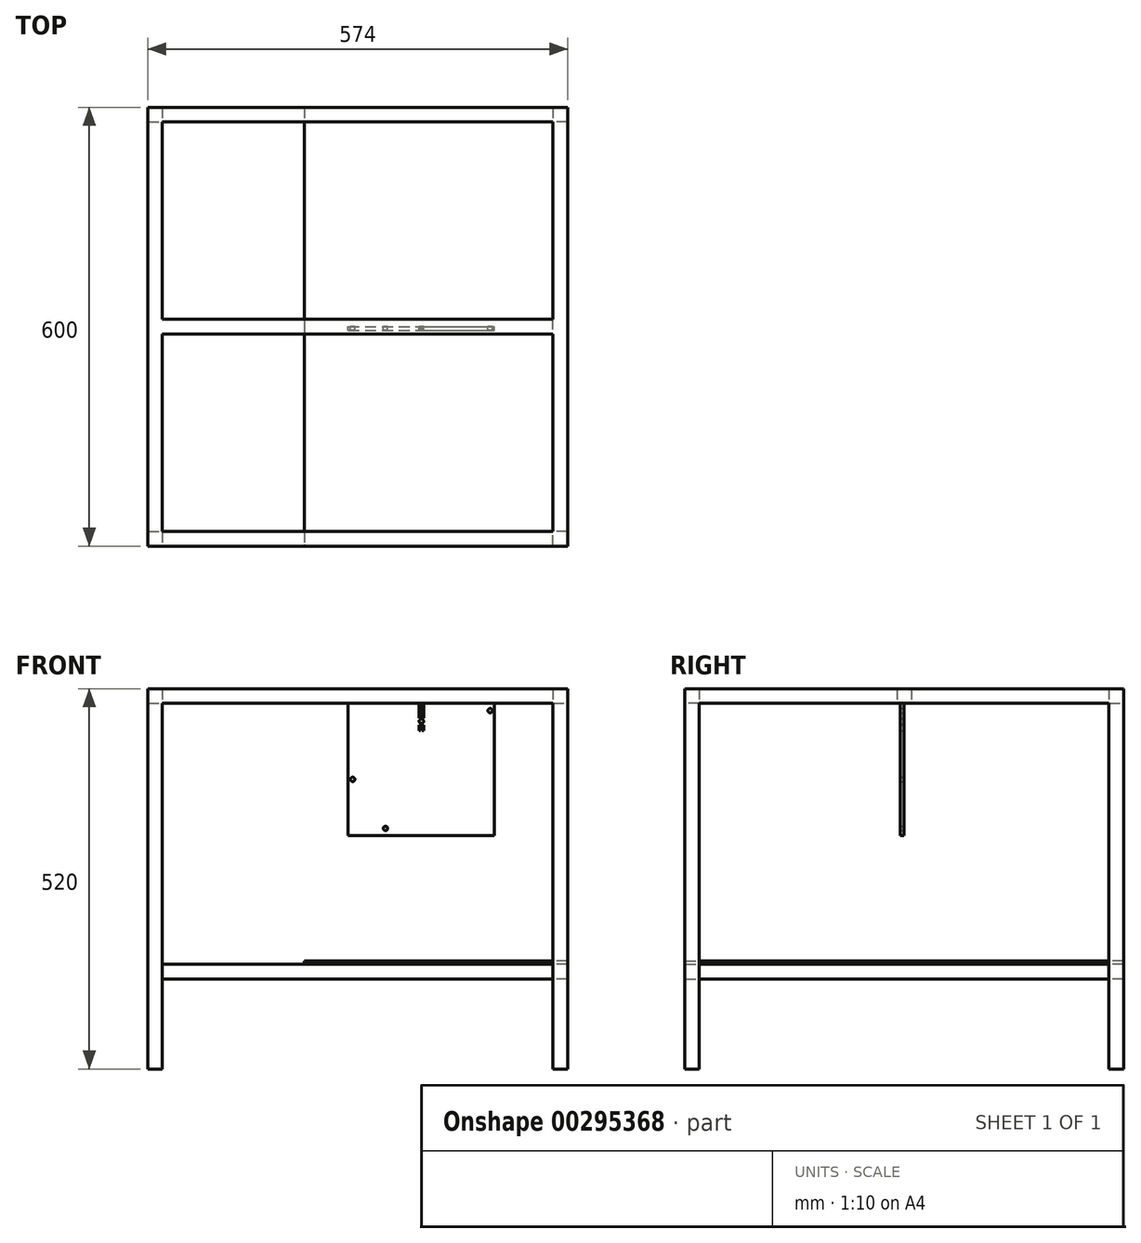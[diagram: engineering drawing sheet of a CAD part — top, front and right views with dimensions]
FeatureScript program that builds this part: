
annotation { "Feature Type Name" : "Feature", "Feature Type Description" : "" }
export const myFeature = defineFeature(function(context is Context, id is Id, definition is map)
    precondition{}
    {
        {
            var Q0;
            Q0=qCreatedBy(makeId("Front.planeOp"),FACE);
            var sketch = newSketch(context, id + "F0", { "sketchPlane" : qUnion([Q0])});
            skCircle(sketch, "E0", {"center": v(0, 0) * mm, "radius": 3 * mm});
            skCircle(sketch, "E1", {"center": v(-45, 67) * mm, "radius": 3 * mm});
            skCircle(sketch, "E2", {"center": v(143, 161) * mm, "radius": 3 * mm});
            skLineSegment(sketch, "E3.bottom", {"start": v(-51, -10) * mm, "end": v(149, -10) * mm});
            skLineSegment(sketch, "E3.top", {"start": v(-51, 171) * mm, "end": v(45.95, 171) * mm});
            skLineSegment(sketch, "E3.left", {"start": v(-51, -10) * mm, "end": v(-51, 171) * mm});
            skLineSegment(sketch, "E3.right", {"start": v(149, -10) * mm, "end": v(149, 171) * mm});
            skCircle(sketch, "E4", {"center": v(49, 146.5) * mm, "radius": 3 * mm});
            skPoint(sketch, "E4.centerSnap0", {"position": v(49, 171) * mm});
            skLineSegment(sketch, "E5.top", {"start": v(45.95, 151) * mm, "end": v(48.05, 151) * mm});
            skLineSegment(sketch, "E5.left", {"start": v(45.95, 171) * mm, "end": v(45.95, 151) * mm});
            skLineSegment(sketch, "E5.right", {"start": v(48.05, 171) * mm, "end": v(48.05, 151) * mm});
            skLineSegment(sketch, "E6.bottom", {"start": v(45.95, 141.5) * mm, "end": v(48.05, 141.5) * mm});
            skLineSegment(sketch, "E6.top", {"start": v(45.95, 133.5) * mm, "end": v(48.05, 133.5) * mm});
            skLineSegment(sketch, "E6.left", {"start": v(45.95, 141.5) * mm, "end": v(45.95, 133.5) * mm});
            skLineSegment(sketch, "E6.right", {"start": v(48.05, 141.5) * mm, "end": v(48.05, 133.5) * mm});
            skLineSegment(sketch, "E7.trimOffspring", {"start": v(48.05, 171) * mm, "end": v(149, 171) * mm});
            skLineSegment(sketch, "E8.MirrorCS", {"start": v(52.05, 133.5) * mm, "end": v(49.95, 133.5) * mm});
            skLineSegment(sketch, "E9.MirrorCS", {"start": v(52.05, 141.5) * mm, "end": v(49.95, 141.5) * mm});
            skLineSegment(sketch, "E10.MirrorCS", {"start": v(49.95, 171) * mm, "end": v(49.95, 151) * mm});
            skLineSegment(sketch, "E11.MirrorCS", {"start": v(52.05, 151) * mm, "end": v(49.95, 151) * mm});
            skLineSegment(sketch, "E12.MirrorCS", {"start": v(52.05, 141.5) * mm, "end": v(52.05, 133.5) * mm});
            skLineSegment(sketch, "E13.MirrorCS", {"start": v(49.95, 141.5) * mm, "end": v(49.95, 133.5) * mm});
            skLineSegment(sketch, "E14.MirrorCS", {"start": v(52.05, 171) * mm, "end": v(52.05, 151) * mm});
            skSolve(sketch);
        }
        {
            var Q0;
            Q0=makeQuery(id+"F0.imprint","IMPRINT",FACE,{"disambiguationData":[TD([[makeQuery(id+"F0.imprint","IMPRINT",EDGE,{"derivedFrom":sQuery(id+"F0.wireOp",EDGE,"E0")}),-1.0]])]});
            extrude(context, id + "F1", {"entities" : qUnion([Q0]), "depth" : 5 * mm});
        }
        {
            var Q0;
            Q0=qCreatedBy(makeId("Top.planeOp"),FACE);
            cPlane(context, id + "F2", {"entities" : qUnion([Q0]), "cplaneType" : CPlaneType.OFFSET, "offset" : 171 * mm, "width" : 150 * mm, "height" : 150 * mm});
        }
        {
            var Q0;
            Q0=qCreatedBy(id+"F2.planeOp",FACE);
            var sketch = newSketch(context, id + "F3", { "sketchPlane" : qUnion([Q0])});
            skLineSegment(sketch, "E15.bottom", {"start": v(249, -300) * mm, "end": v(229, -300) * mm});
            skLineSegment(sketch, "E15.top", {"start": v(249, 300) * mm, "end": v(229, 300) * mm});
            skLineSegment(sketch, "E15.left", {"start": v(249, -300) * mm, "end": v(249, 300) * mm});
            skLineSegment(sketch, "E15.right", {"start": v(229, -280) * mm, "end": v(229, 280) * mm});
            skLineSegment(sketch, "E16.bottom", {"start": v(229, 300) * mm, "end": v(-305, 300) * mm});
            skLineSegment(sketch, "E16.top", {"start": v(229, 280) * mm, "end": v(-305, 280) * mm});
            skLineSegment(sketch, "E17.bottom", {"start": v(229, -300) * mm, "end": v(-305, -300) * mm});
            skLineSegment(sketch, "E17.top", {"start": v(229, -280) * mm, "end": v(-305, -280) * mm});
            skLineSegment(sketch, "E18.bottom", {"start": v(-305, 300) * mm, "end": v(-325, 300) * mm});
            skLineSegment(sketch, "E18.top", {"start": v(-305, -300) * mm, "end": v(-325, -300) * mm});
            skLineSegment(sketch, "E18.left", {"start": v(-305, 280) * mm, "end": v(-305, -280) * mm});
            skLineSegment(sketch, "E18.right", {"start": v(-325, 300) * mm, "end": v(-325, -300) * mm});
            skPoint(sketch, "E19", {"position": v(249, 0) * mm});
            skLineSegment(sketch, "E20.bottom", {"start": v(229, -10) * mm, "end": v(-305, -10) * mm});
            skLineSegment(sketch, "E20.top", {"start": v(229, 10) * mm, "end": v(-305, 10) * mm});
            skLineSegment(sketch, "E20.left", {"start": v(229, -10) * mm, "end": v(229, 10) * mm});
            skLineSegment(sketch, "E20.right", {"start": v(-305, -10) * mm, "end": v(-305, 10) * mm});
            skPoint(sketch, "E20.middle", {"position": v(-38, 0) * mm});
            skSolve(sketch);
        }
        {
            var Q0;
            Q0=qSketchRegion(id+"F3",true);
            var Q1;
            Q1=makeQuery(id+"F3.imprint","IMPRINT",FACE,{"disambiguationData":[TD([[makeQuery(id+"F3.imprint","IMPRINT",EDGE,{"derivedFrom":sQuery(id+"F3.wireOp",EDGE,"E20.bottom")}),-1.0]])]});
            extrude(context, id + "F4", {"entities" : qUnion([Q0, Q1]), "operationType" : NewBodyOperationType.ADD, "depth" : 20 * mm});
        }
        {
            var Q0;
            Q0=makeQuery(id+"F4.opExtrude","CAP_FACE",FACE,{"disambiguationData":[OSD([sQuery(id+"F3.wireOp",EDGE,"E15.bottom"),sQuery(id+"F3.wireOp",EDGE,"E15.top"),sQuery(id+"F3.wireOp",EDGE,"E15.left"),sQuery(id+"F3.wireOp",EDGE,"E15.right"),sQuery(id+"F3.wireOp",EDGE,"7mnNWSTb-ftgJ-FYnv-rSfW-03W7qfMdHJeY.bottom"),sQuery(id+"F3.wireOp",EDGE,"7mnNWSTb-ftgJ-FYnv-rSfW-03W7qfMdHJeY.top"),sQuery(id+"F3.wireOp",EDGE,"yphk7Mg7-LXwZ-R6qe-Yzbn-fpSbBpRDTs4J.bottom"),sQuery(id+"F3.wireOp",EDGE,"yphk7Mg7-LXwZ-R6qe-Yzbn-fpSbBpRDTs4J.top"),sQuery(id+"F3.wireOp",EDGE,"yphk7Mg7-LXwZ-R6qe-Yzbn-fpSbBpRDTs4J.left"),sQuery(id+"F3.wireOp",EDGE,"yphk7Mg7-LXwZ-R6qe-Yzbn-fpSbBpRDTs4J.right"),sQuery(id+"F3.wireOp",EDGE,"9GNo11h2-buUj-PFzF-0UOW-2sDmyF7RkODV.bottom"),sQuery(id+"F3.wireOp",EDGE,"9GNo11h2-buUj-PFzF-0UOW-2sDmyF7RkODV.top")])],"isStart":true});
            var sketch = newSketch(context, id + "F5", { "sketchPlane" : qUnion([Q0])});
            skLineSegment(sketch, "E21.bottom", {"start": v(-325, 300) * mm, "end": v(-305, 300) * mm});
            skLineSegment(sketch, "E21.top", {"start": v(-325, 280) * mm, "end": v(-305, 280) * mm});
            skLineSegment(sketch, "E21.left", {"start": v(-325, 300) * mm, "end": v(-325, 280) * mm});
            skLineSegment(sketch, "E21.right", {"start": v(-305, 300) * mm, "end": v(-305, 280) * mm});
            skLineSegment(sketch, "E22.bottom", {"start": v(-325, -300) * mm, "end": v(-305, -300) * mm});
            skLineSegment(sketch, "E22.top", {"start": v(-325, -280) * mm, "end": v(-305, -280) * mm});
            skLineSegment(sketch, "E22.left", {"start": v(-325, -300) * mm, "end": v(-325, -280) * mm});
            skLineSegment(sketch, "E22.right", {"start": v(-305, -300) * mm, "end": v(-305, -280) * mm});
            skLineSegment(sketch, "E23.bottom", {"start": v(229, -280) * mm, "end": v(249, -280) * mm});
            skLineSegment(sketch, "E23.top", {"start": v(229, -300) * mm, "end": v(249, -300) * mm});
            skLineSegment(sketch, "E23.left", {"start": v(229, -280) * mm, "end": v(229, -300) * mm});
            skLineSegment(sketch, "E23.right", {"start": v(249, -280) * mm, "end": v(249, -300) * mm});
            skLineSegment(sketch, "E24.bottom", {"start": v(229, 280) * mm, "end": v(249, 280) * mm});
            skLineSegment(sketch, "E24.top", {"start": v(229, 300) * mm, "end": v(249, 300) * mm});
            skLineSegment(sketch, "E24.left", {"start": v(229, 280) * mm, "end": v(229, 300) * mm});
            skLineSegment(sketch, "E24.right", {"start": v(249, 280) * mm, "end": v(249, 300) * mm});
            skSolve(sketch);
        }
        {
            var Q0;
            Q0=qSketchRegion(id+"F5",true);
            extrude(context, id + "F6", {"entities" : qUnion([Q0]), "operationType" : NewBodyOperationType.ADD, "depth" : 500 * mm});
        }
        {
            var Q0;
            Q0=qCreatedBy(makeId("Top.planeOp"),FACE);
            cPlane(context, id + "F7", {"entities" : qUnion([Q0]), "cplaneType" : CPlaneType.OFFSET, "offset" : 186 * mm, "oppositeDirection" : true, "width" : 150 * mm, "height" : 150 * mm});
        }
        {
            var Q0;
            Q0=qCreatedBy(id+"F7.planeOp",FACE);
            var sketch = newSketch(context, id + "F8", { "sketchPlane" : qUnion([Q0])});
            skPoint(sketch, "E25.middle", {"position": v(69, 0) * mm});
            skLineSegment(sketch, "E26.top", {"start": v(229, 300) * mm, "end": v(-111, 300) * mm});
            skLineSegment(sketch, "E27.top", {"start": v(229, -300) * mm, "end": v(-111, -300) * mm});
            skLineSegment(sketch, "E28", {"start": v(-111, 300) * mm, "end": v(-111, -300) * mm});
            skLineSegment(sketch, "E29", {"start": v(249, 280) * mm, "end": v(249, -280) * mm});
            skPoint(sketch, "E30", {"position": v(249, 0) * mm});
            skLineSegment(sketch, "E31.top", {"start": v(249, 280) * mm, "end": v(229, 280) * mm});
            skLineSegment(sketch, "E31.right", {"start": v(229, 300) * mm, "end": v(229, 280) * mm});
            skPoint(sketch, "E31.left.start.orphan", {"position": v(249, 300) * mm});
            skLineSegment(sketch, "E32.top", {"start": v(249, -280) * mm, "end": v(229, -280) * mm});
            skLineSegment(sketch, "E32.right", {"start": v(229, -300) * mm, "end": v(229, -280) * mm});
            skPoint(sketch, "E32.left.start.orphan", {"position": v(249, -300) * mm});
            skSolve(sketch);
        }
        {
            var Q0;
            Q0 = qSketchRegion(id + "F8", true);
            extrude(context, id + "F9", {"entities" : qUnion([Q0]), "depth" : 5 * mm});
        }
        {
            var Q0;
            Q0=makeQuery(id+"F9.opExtrude","CAP_FACE",FACE,{"disambiguationData":[OSD([sQuery(id+"F8.wireOp",EDGE,"E26.top"),sQuery(id+"F8.wireOp",EDGE,"E27.top"),sQuery(id+"F8.wireOp",EDGE,"E28"),sQuery(id+"F8.wireOp",EDGE,"E29"),sQuery(id+"F8.wireOp",EDGE,"E31.top"),sQuery(id+"F8.wireOp",EDGE,"E31.right"),sQuery(id+"F8.wireOp",EDGE,"E32.top"),sQuery(id+"F8.wireOp",EDGE,"E32.right")])],"isStart":true});
            var sketch = newSketch(context, id + "F10", { "sketchPlane" : qUnion([Q0])});
            skPoint(sketch, "E33.oppositeSnap0", {"position": v(239, 280) * mm});
            skLineSegment(sketch, "E34.bottom", {"start": v(229, 280) * mm, "end": v(249, 280) * mm});
            skLineSegment(sketch, "E34.top", {"start": v(229, -280) * mm, "end": v(249, -280) * mm});
            skLineSegment(sketch, "E34.left", {"start": v(229, 280) * mm, "end": v(229, -280) * mm});
            skLineSegment(sketch, "E34.right", {"start": v(249, 280) * mm, "end": v(249, -280) * mm});
            skLineSegment(sketch, "E35.bottom", {"start": v(229, 280) * mm, "end": v(-305, 280) * mm});
            skLineSegment(sketch, "E35.top", {"start": v(229, 300) * mm, "end": v(-305, 300) * mm});
            skLineSegment(sketch, "E35.left", {"start": v(229, 280) * mm, "end": v(229, 300) * mm});
            skLineSegment(sketch, "E35.right", {"start": v(-305, 280) * mm, "end": v(-305, 300) * mm});
            skLineSegment(sketch, "E36.bottom", {"start": v(229, -300) * mm, "end": v(-305, -300) * mm});
            skLineSegment(sketch, "E36.top", {"start": v(229, -280) * mm, "end": v(-305, -280) * mm});
            skLineSegment(sketch, "E36.left", {"start": v(229, -300) * mm, "end": v(229, -280) * mm});
            skLineSegment(sketch, "E36.right", {"start": v(-305, -300) * mm, "end": v(-305, -280) * mm});
            skSolve(sketch);
        }
        {
            var Q0;
            Q0 = qSketchRegion(id + "F10", true);
            extrude(context, id + "F11", {"entities" : qUnion([Q0]), "depth" : 20 * mm});
        }
    });
